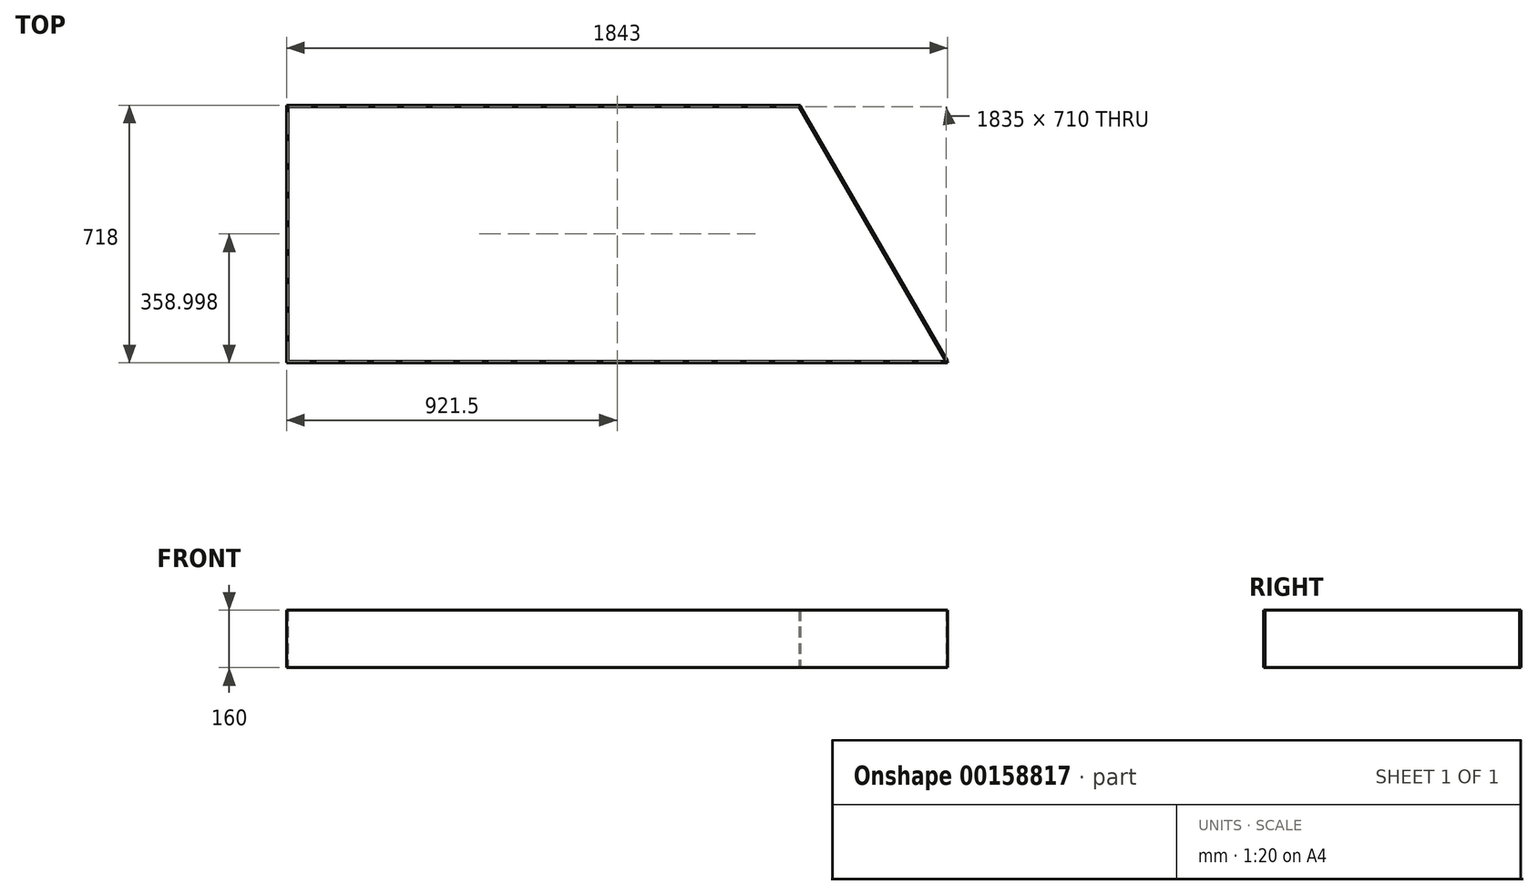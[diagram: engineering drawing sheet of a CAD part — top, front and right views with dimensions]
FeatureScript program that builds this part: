
annotation { "Feature Type Name" : "Feature", "Feature Type Description" : "" }
export const myFeature = defineFeature(function(context is Context, id is Id, definition is map)
    precondition{}
    {
        {
            var Q0;
            Q0=qCreatedBy(makeId("Top.planeOp"),FACE);
            var sketch = newSketch(context, id + "F0", { "sketchPlane" : qUnion([Q0])});
            skLineSegment(sketch, "E0", {"start": v(0, 20.82) * mm, "end": v(0, 730.82) * mm});
            skLineSegment(sketch, "E1", {"start": v(0, 730.82) * mm, "end": v(1425, 730.82) * mm});
            skLineSegment(sketch, "E2", {"start": v(1425, 730.82) * mm, "end": v(1835, 20.82) * mm});
            skLineSegment(sketch, "E3", {"start": v(0, 20.82) * mm, "end": v(1835, 20.82) * mm});
            skLineSegment(sketch, "E4", {"start": v(0, 16.82) * mm, "end": v(1835, 16.82) * mm});
            skLineSegment(sketch, "E5", {"start": v(1839, 20.82) * mm, "end": v(1429, 730.82) * mm});
            skLineSegment(sketch, "E6", {"start": v(1425, 734.82) * mm, "end": v(0, 734.82) * mm});
            skLineSegment(sketch, "E7", {"start": v(-4, 730.82) * mm, "end": v(-4, 20.82) * mm});
            skLineSegment(sketch, "E8", {"start": v(-4, 20.82) * mm, "end": v(-4, 16.82) * mm});
            skLineSegment(sketch, "E9", {"start": v(-4, 16.82) * mm, "end": v(0, 16.82) * mm});
            skLineSegment(sketch, "E10", {"start": v(-4, 730.82) * mm, "end": v(-4, 734.82) * mm});
            skLineSegment(sketch, "E11", {"start": v(-4, 734.82) * mm, "end": v(0, 734.82) * mm});
            skLineSegment(sketch, "E12", {"start": v(1835, 16.82) * mm, "end": v(1839, 16.82) * mm});
            skLineSegment(sketch, "E13", {"start": v(1839, 16.82) * mm, "end": v(1839, 20.82) * mm});
            skPoint(sketch, "E14.start.orphan", {"position": v(1426.7, 734.82) * mm});
            skLineSegment(sketch, "E15", {"start": v(1426.7, 734.82) * mm, "end": v(1425, 734.82) * mm});
            skPoint(sketch, "E16.end.orphan", {"position": v(1429, 734.82) * mm});
            skLineSegment(sketch, "E17", {"start": v(1426.7, 734.82) * mm, "end": v(1429, 734.82) * mm});
            skLineSegment(sketch, "E18", {"start": v(1429, 730.82) * mm, "end": v(1429, 734.82) * mm});
            skSolve(sketch);
        }
        {
            var Q0;
            Q0=qSketchRegion(id+"F0",true);
            extrude(context, id + "F1", {"entities" : qUnion([Q0]), "depth" : 160 * mm});
        }
    });
